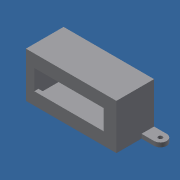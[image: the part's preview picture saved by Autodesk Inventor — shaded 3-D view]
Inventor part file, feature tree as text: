
AUTODESK INVENTOR PART (.ipt)
format: ipt  version: 2021 (Build 250183000, 183)  size: 122,368 bytes
history: native  units: mm
features: extrude x3, sketch x3
ambient origin geometry x8: Origin, YZ Plane, XZ Plane, XY Plane, X Axis, Y Axis, Z Axis, Center Point
bodies: Solid1 (feature_tree)
feature tree (6):
  extrude  "Extrusion1"  Depth=44.0mm
  extrude  "Extrusion2"  Depth=5.0mm
  extrude  "Extrusion3"  Depth=5.0mm
  sketch  "Sketch1"  dims[d0=98.0mm d1=44.0mm]
  sketch  "Sketch2"  dims[d2=5.0mm d3=5.0mm]
  sketch  "Sketch3"  dims[d4=5.0mm d5=5.0mm d6=40.0mm d7=0.0mm d8=5.0mm d9=0.0mm d10=10.0mm d11=15.0mm d12=15.0mm d13=15.0mm d14=15.0mm d15=15.0mm d16=5.0mm d17=5.0mm d18=0.0mm]
